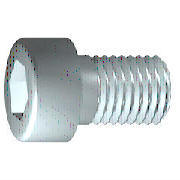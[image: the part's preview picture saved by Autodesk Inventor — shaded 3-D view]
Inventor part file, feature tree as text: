
AUTODESK INVENTOR PART (.ipt)
format: ipt  version: 2017.1 (Build 211199000, 199)  size: 199,680 bytes
history: native  units: mm (DEFAULTED — no unit token found)
features: sketch x2, extrude x1, plane x1, fillet x1
ambient origin geometry x7: Origin, YZ Plane, XY Plane, X Axis, Y Axis, Z Axis, Center Point
bodies: Solid1 (feature_tree), Body (feature_tree)
feature tree (5):
  extrude  "Slot"  Depth=3.5052mm
  plane  "Work Plane1"
  fillet  "Fillet2"  Radius=3.5052mm
  sketch  "Sketch1"  dims[d1=7.540552mm d2=1.984348mm d3=3.5052mm]
  sketch  "Sketch2"  dims[d4=1.6256mm d5=60.0deg d6=3.5052mm d7=3.5052mm d8=3.196904mm d9=5.7404mm d10=90.0deg d11=10.0mm d12=0.0mm d13=7.540552mm d14=0.0mm d15=0.47244mm d16=0.47244mm d17=0.3302mm d19=0.0mm d26=9.525mm d27=45.0deg d28=0.0mm d29=0.0mm d30=0.127mm]
